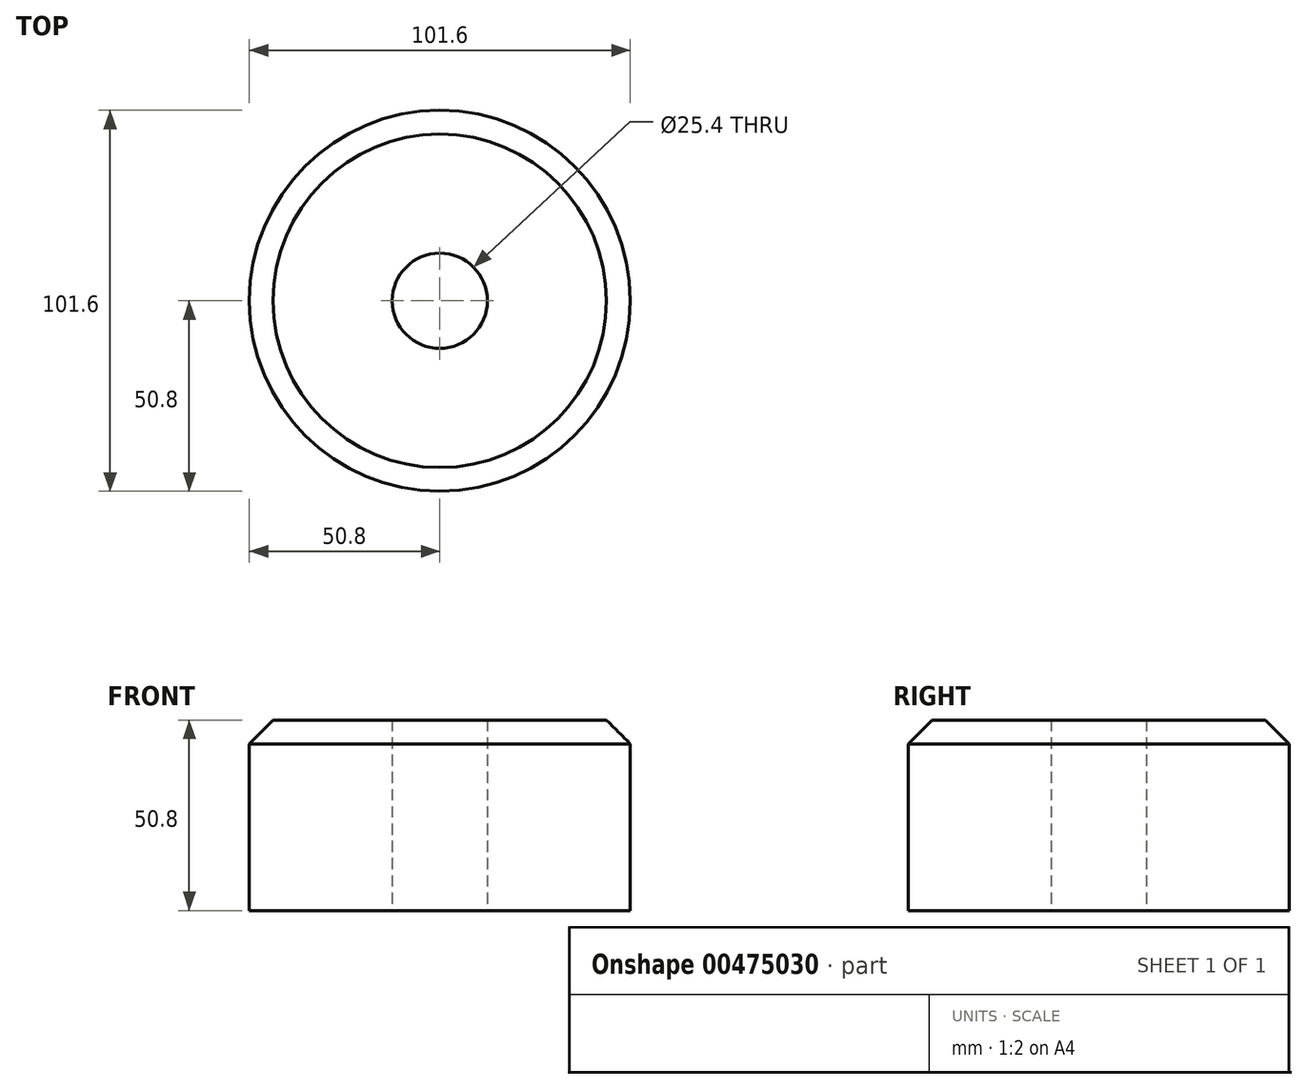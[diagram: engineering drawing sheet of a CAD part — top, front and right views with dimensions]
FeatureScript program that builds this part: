
annotation { "Feature Type Name" : "Feature", "Feature Type Description" : "" }
export const myFeature = defineFeature(function(context is Context, id is Id, definition is map)
    precondition{}
    {
        {
            var Q0;
            Q0=qCreatedBy(makeId("Top.planeOp"),FACE);
            var sketch = newSketch(context, id + "F0", { "sketchPlane" : qUnion([Q0])});
            skCircle(sketch, "E0", {"center": v(0, 0) * mm, "radius": 50.8 * mm});
            skCircle(sketch, "E1", {"center": v(0, 0) * mm, "radius": 12.7 * mm});
            skSolve(sketch);
        }
        {
            var Q0;
            Q0=makeQuery(id+"F0.imprint","IMPRINT",FACE,{"disambiguationData":[TD([[makeQuery(id+"F0.imprint","IMPRINT",EDGE,{"derivedFrom":sQuery(id+"F0.wireOp",EDGE,"E0")}),1.0]])]});
            var Q1;
            Q1=sQuery(id+"F0.wireOp",EDGE,"E0");
            extrude(context, id + "F1", {"entities" : qUnion([Q0]), "surfaceEntities" : qUnion([Q1]), "depth" : 25.4 * mm});
        }
        {
            var Q0;
            Q0=makeQuery(id+"F1.opExtrude","CAP_EDGE",EDGE,{"disambiguationData":[OSD([sQuery(id+"F0.wireOp",EDGE,"E0")])],"isStart":false});
            chamfer(context, id + "F2", {"entities" : qUnion([Q0]), "width" : 6.35 * mm, "tangentPropagation" : true});
        }
        {
            var Q0;
            Q0=makeQuery(id+"F0.imprint","IMPRINT",FACE,{"disambiguationData":[TD([[makeQuery(id+"F0.imprint","IMPRINT",EDGE,{"derivedFrom":sQuery(id+"F0.wireOp",EDGE,"E0")}),1.0]])]});
            extrude(context, id + "F3", {"entities" : qUnion([Q0]), "operationType" : NewBodyOperationType.ADD, "oppositeDirection" : true, "depth" : 25.4 * mm});
        }
    });
